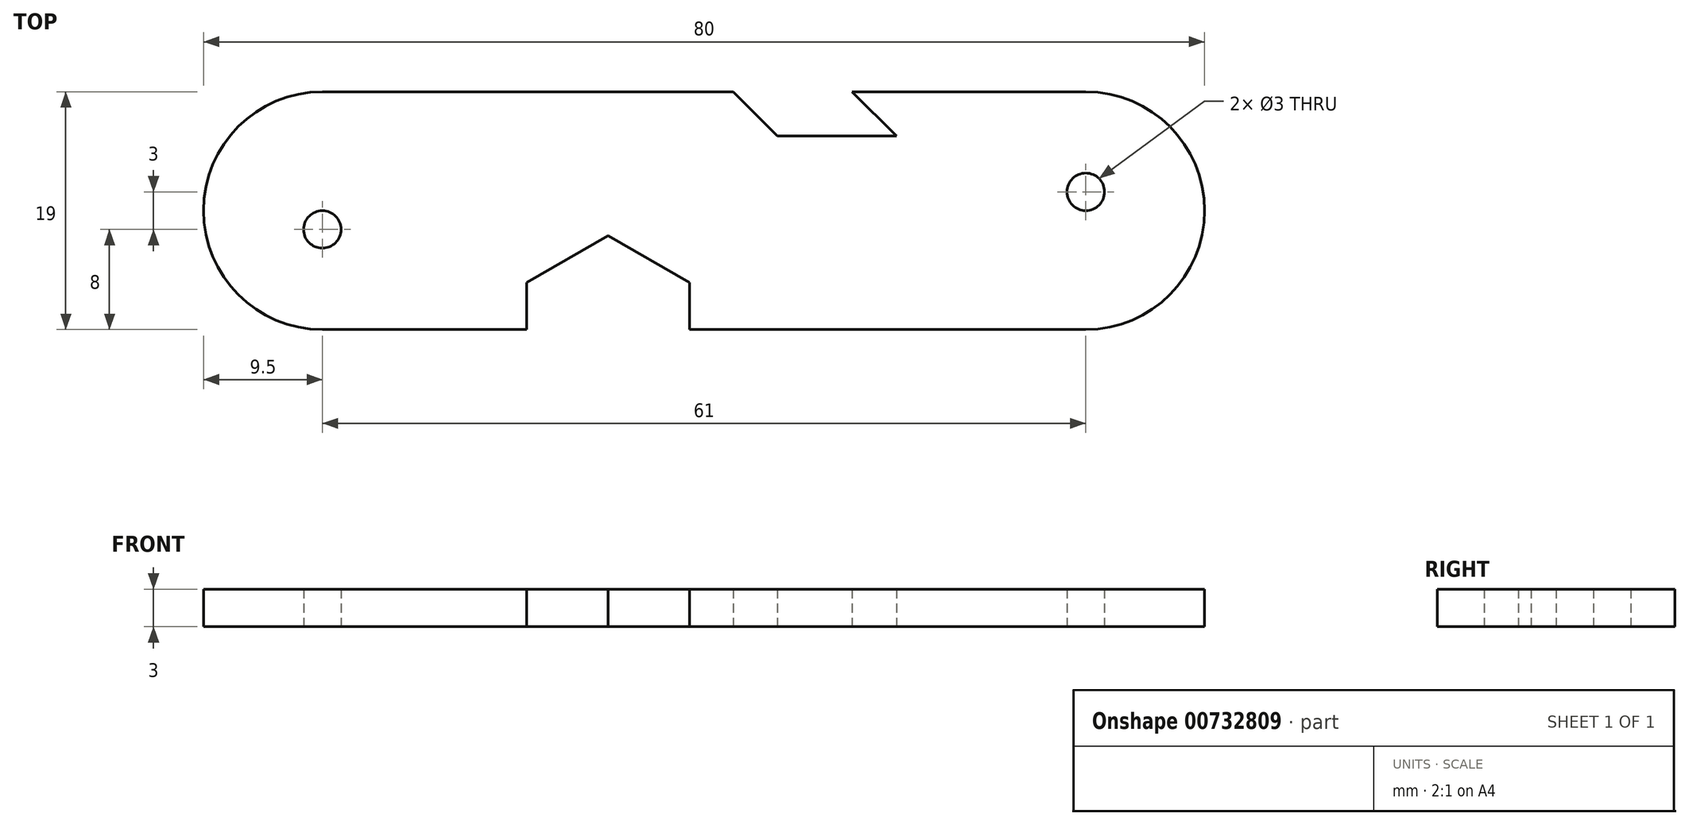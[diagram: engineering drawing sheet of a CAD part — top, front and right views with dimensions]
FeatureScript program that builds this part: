
annotation { "Feature Type Name" : "Feature", "Feature Type Description" : "" }
export const myFeature = defineFeature(function(context is Context, id is Id, definition is map)
    precondition{}
    {
        {
            var Q0;
            Q0=qCreatedBy(makeId("Top.planeOp"),FACE);
            var sketch = newSketch(context, id + "F0", { "sketchPlane" : qUnion([Q0])});
            skArc(sketch, "E0", {"start": v(-29.33, 9.5) * mm, "mid": v(-38.83, 0) * mm, "end": v(-29.33, -9.5) * mm});
            skArc(sketch, "E1", {"start": v(31.67, -9.5) * mm, "mid": v(41.17, 0) * mm, "end": v(31.67, 9.5) * mm});
            skLineSegment(sketch, "E2", {"start": v(-29.33, -9.5) * mm, "end": v(-18, -9.5) * mm});
            skLineSegment(sketch, "E3", {"start": v(31.67, 9.5) * mm, "end": v(18, 9.5) * mm});
            skCircle(sketch, "E4", {"center": v(-29.33, -1.5) * mm, "radius": 1.5 * mm});
            skCircle(sketch, "E5", {"center": v(31.67, 1.5) * mm, "radius": 1.5 * mm});
            skLineSegment(sketch, "E6.trimOffspring", {"start": v(0, 9.5) * mm, "end": v(-29.33, 9.5) * mm});
            skLineSegment(sketch, "E7.trimOffspring", {"start": v(0, -9.5) * mm, "end": v(31.67, -9.5) * mm});
            skLineSegment(sketch, "E8", {"start": v(-18, -9.5) * mm, "end": v(-13, -9.5) * mm});
            skLineSegment(sketch, "E9", {"start": v(0, 9.5) * mm, "end": v(3.5, 9.5) * mm});
            skCircle(sketch, "E10.cCircle", {"center": v(-6.5, -9.5) * mm, "radius": 6.5 * mm, "construction": true});
            skLineSegment(sketch, "E10.0", {"start": v(-13, -9.5) * mm, "end": v(-13, -5.75) * mm});
            skLineSegment(sketch, "E10.1", {"start": v(-13, -5.75) * mm, "end": v(-6.5, -2) * mm});
            skLineSegment(sketch, "E10.2", {"start": v(-6.5, -2) * mm, "end": v(0, -5.75) * mm});
            skLineSegment(sketch, "E10.3", {"start": v(0, -5.75) * mm, "end": v(0, -9.5) * mm});
            skPoint(sketch, "E10.0.midPoint", {"position": v(-13, -9.5) * mm});
            skPoint(sketch, "E11.orphan", {"position": v(-13, -13.25) * mm});
            skLineSegment(sketch, "E12", {"start": v(13, 9.5) * mm, "end": v(16.54, 5.96) * mm});
            skLineSegment(sketch, "E13", {"start": v(16.54, 5.96) * mm, "end": v(7.04, 5.96) * mm});
            skLineSegment(sketch, "E14", {"start": v(7.04, 5.96) * mm, "end": v(3.5, 9.5) * mm});
            skLineSegment(sketch, "E15.trimOffspring", {"start": v(13, 9.5) * mm, "end": v(18, 9.5) * mm});
            skSolve(sketch);
        }
        {
            var Q0;
            Q0 = qSketchRegion(id + "F0", true);
            extrude(context, id + "F1", {"entities" : qUnion([Q0]), "depth" : 3 * mm, "offsetDistance" : 25 * mm});
        }
    });
